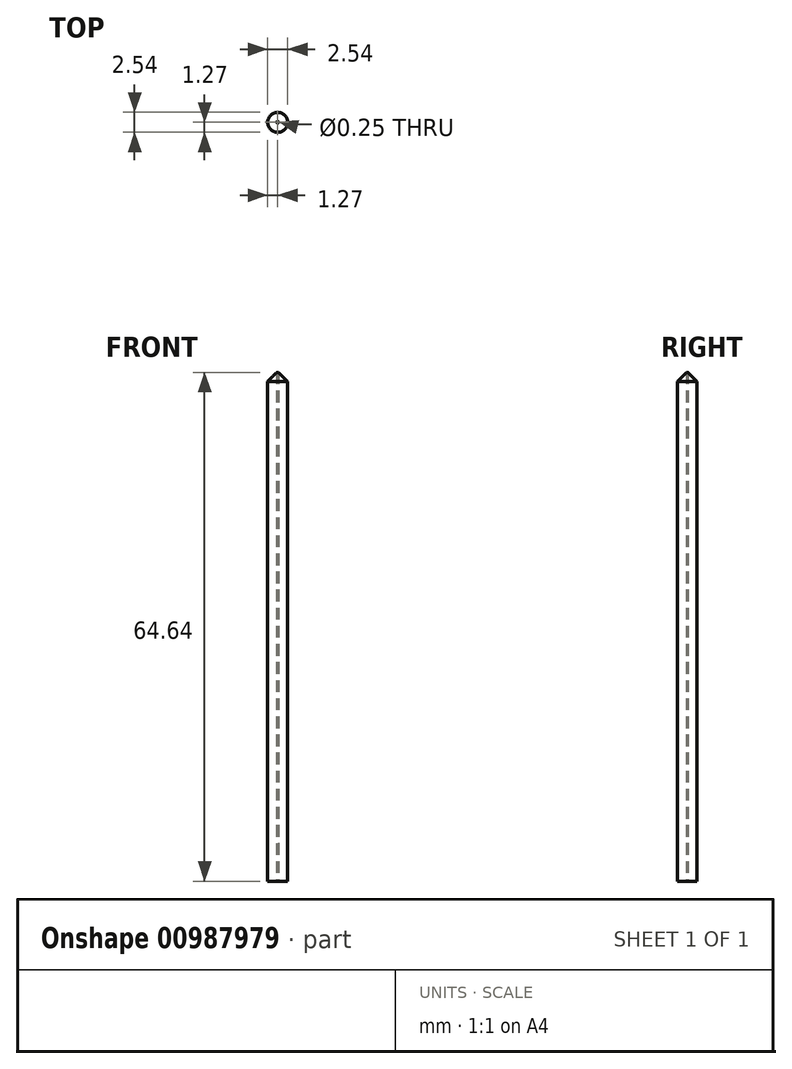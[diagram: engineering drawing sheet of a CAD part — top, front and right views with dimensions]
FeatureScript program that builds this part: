
annotation { "Feature Type Name" : "Feature", "Feature Type Description" : "" }
export const myFeature = defineFeature(function(context is Context, id is Id, definition is map)
    precondition{}
    {
        {
            var Q0;
            Q0=qCreatedBy(makeId("Top.planeOp"),FACE);
            var sketch = newSketch(context, id + "F0", { "sketchPlane" : qUnion([Q0])});
            skCircle(sketch, "E0", {"center": v(0, 0) * mm, "radius": 1.27 * mm});
            skSolve(sketch);
        }
        {
            var Q0;
            Q0 = qSketchRegion(id + "F0", true);
            extrude(context, id + "F1", {"entities" : qUnion([Q0]), "depth" : 64.77 * mm, "offsetDistance" : 25.4 * mm});
        }
        {
            var Q0;
            Q0=makeQuery(id+"F1.opExtrude","CAP_EDGE",EDGE,{"disambiguationData":[OSD([sQuery(id+"F0.wireOp",EDGE,"E0")])],"isStart":false});
            chamfer(context, id + "F2", {"entities" : qUnion([Q0]), "width" : 1.27 * mm, "tangentPropagation" : true});
        }
        {
            var Q0;
            Q0=makeQuery(id+"F1.opExtrude","CAP_FACE",FACE,{"disambiguationData":[OSD([sQuery(id+"F0.wireOp",EDGE,"E0")])],"isStart":true});
            var sketch = newSketch(context, id + "F3", { "sketchPlane" : qUnion([Q0])});
            skCircle(sketch, "E1", {"center": v(0, 0) * mm, "radius": 0.13 * mm});
            skSolve(sketch);
        }
        {
            var Q0;
            Q0 = qSketchRegion(id + "F3", true);
            extrude(context, id + "F4", {"entities" : qUnion([Q0]), "operationType" : NewBodyOperationType.REMOVE, "endBound" : BoundingType.THROUGH_ALL, "oppositeDirection" : true, "depth" : 25.4 * mm, "offsetDistance" : 25.4 * mm});
        }
    });
